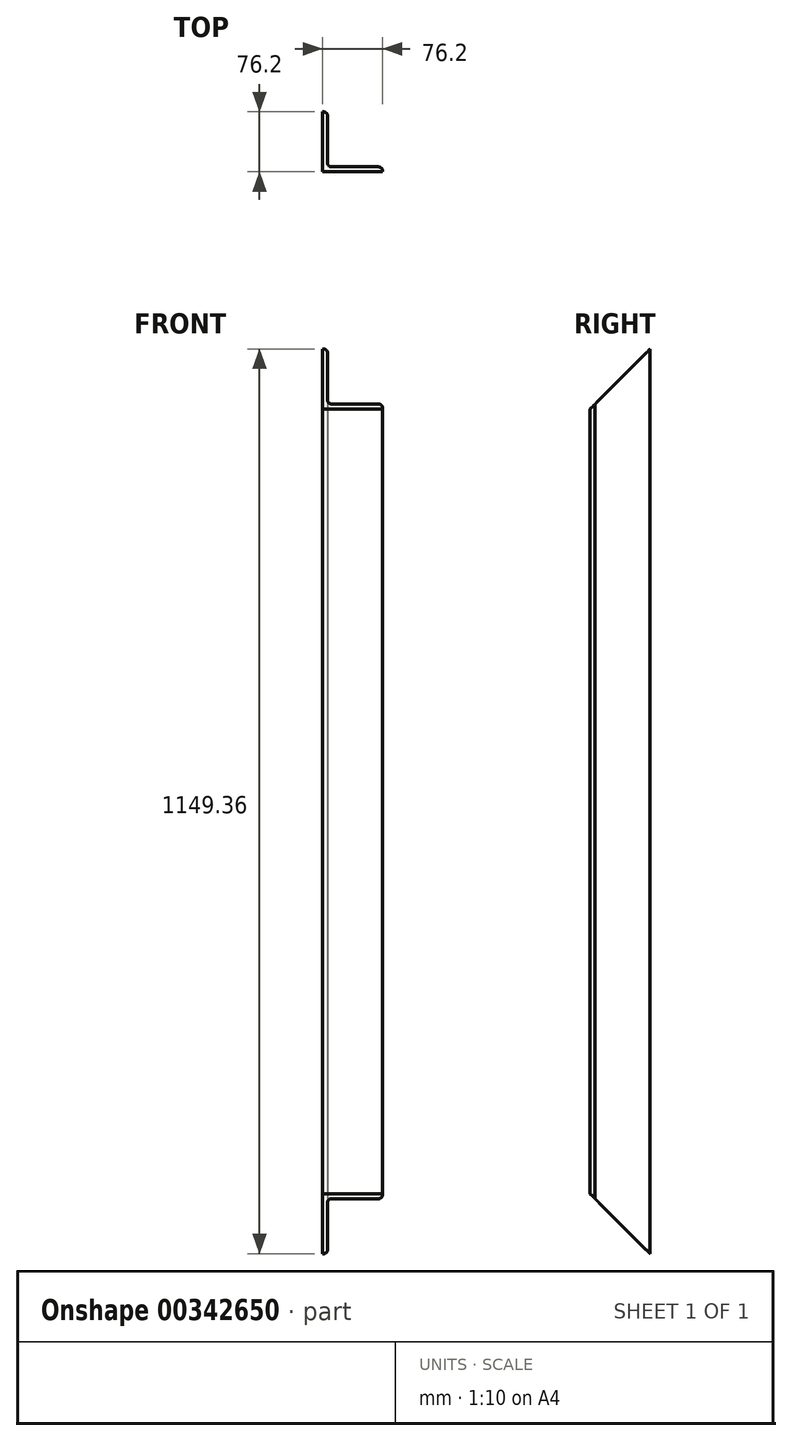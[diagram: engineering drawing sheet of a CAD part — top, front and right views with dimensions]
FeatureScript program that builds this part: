
annotation { "Feature Type Name" : "Feature", "Feature Type Description" : "" }
export const myFeature = defineFeature(function(context is Context, id is Id, definition is map)
    precondition{}
    {
        {
            var Q0;
            Q0=qCreatedBy(makeId("Top.planeOp"),FACE);
            var sketch = newSketch(context, id + "F0", { "sketchPlane" : qUnion([Q0])});
            skLineSegment(sketch, "E0", {"start": v(0, 0) * mm, "end": v(0, 76.2) * mm});
            skLineSegment(sketch, "E1", {"start": v(0, 76.2) * mm, "end": v(6.35, 76.2) * mm});
            skLineSegment(sketch, "E2", {"start": v(6.35, 76.2) * mm, "end": v(6.35, 6.35) * mm});
            skLineSegment(sketch, "E3", {"start": v(6.35, 6.35) * mm, "end": v(76.2, 6.35) * mm});
            skLineSegment(sketch, "E4", {"start": v(76.2, 6.35) * mm, "end": v(76.2, 0) * mm});
            skLineSegment(sketch, "E5", {"start": v(76.2, 0) * mm, "end": v(0, 0) * mm});
            skSolve(sketch);
        }
        {
            var Q0;
            Q0 = qSketchRegion(id + "F0", true);
            extrude(context, id + "F1", {"entities" : qUnion([Q0]), "endBound" : BoundingType.SYMMETRIC, "depth" : 1149.35 * mm});
        }
        {
            var Q0;
            Q0=makeQuery(id+"F1.opExtrude","SWEPT_FACE",FACE,{"disambiguationData":[OSD([sQuery(id+"F0.wireOp",EDGE,"E0")])]});
            var sketch = newSketch(context, id + "F2", { "sketchPlane" : qUnion([Q0])});
            skLineSegment(sketch, "E6", {"start": v(0, -574.68) * mm, "end": v(0, -371.48) * mm});
            skLineSegment(sketch, "E7", {"start": v(0, 574.68) * mm, "end": v(0, 371.48) * mm});
            skPoint(sketch, "E8.0", {"position": v(-76.2, -574.68) * mm});
            skPoint(sketch, "E9.0", {"position": v(-76.2, 574.68) * mm});
            skLineSegment(sketch, "E10", {"start": v(-76.2, -574.68) * mm, "end": v(58.56, -439.91) * mm});
            skLineSegment(sketch, "E11", {"start": v(-76.2, 574.68) * mm, "end": v(114.23, 384.25) * mm});
            skSolve(sketch);
        }
        {
            var Q0;
            Q0 = qSketchRegion(id + "F2", true);
            var Q1;
            {var subQ1=sQuery(id+"F0.wireOp",EDGE,"E0");var subQ2=makeQuery(id+"F1.opExtrude","CAP_EDGE",EDGE,{"disambiguationData":[OSD([subQ1])],"isStart":true});Q1=makeQuery(id+"F2.imprint","IMPRINT",FACE,{"disambiguationData":[TD([[makeQuery(id+"F2.imprint","IMPRINT",EDGE,{"derivedFrom":subQ2}),-1.0]])]});}
            var Q2;
            {var subQ1=sQuery(id+"F0.wireOp",EDGE,"E0");var subQ2=makeQuery(id+"F1.opExtrude","CAP_EDGE",EDGE,{"disambiguationData":[OSD([subQ1])],"isStart":false});Q2=makeQuery(id+"F2.imprint","IMPRINT",FACE,{"disambiguationData":[TD([[makeQuery(id+"F2.imprint","IMPRINT",EDGE,{"derivedFrom":subQ2}),1.0]])]});}
            extrude(context, id + "F3", {"entities" : qUnion([Q0, Q1, Q2]), "operationType" : NewBodyOperationType.REMOVE, "oppositeDirection" : true, "depth" : 76.2 * mm});
        }
        {
            var Q0;
            Q0=makeQuery(id+"F1.opExtrude","SWEPT_EDGE",EDGE,{"disambiguationData":[OSD([sQuery(id+"F0.wireOp",EDGE,"E1"),sQuery(id+"F0.wireOp",EDGE,"E2")])]});
            var Q1;
            Q1=makeQuery(id+"F1.opExtrude","SWEPT_EDGE",EDGE,{"disambiguationData":[OSD([sQuery(id+"F0.wireOp",EDGE,"E2"),sQuery(id+"F0.wireOp",EDGE,"E3")])]});
            var Q2;
            Q2=makeQuery(id+"F1.opExtrude","SWEPT_EDGE",EDGE,{"disambiguationData":[OSD([sQuery(id+"F0.wireOp",EDGE,"E3"),sQuery(id+"F0.wireOp",EDGE,"E4")])]});
            fillet(context, id + "F4", {"entities" : qUnion([Q0, Q1, Q2]), "radius" : 5.08 * mm, "tangentPropagation" : true, "allowEdgeOverflow" : false});
        }
    });
